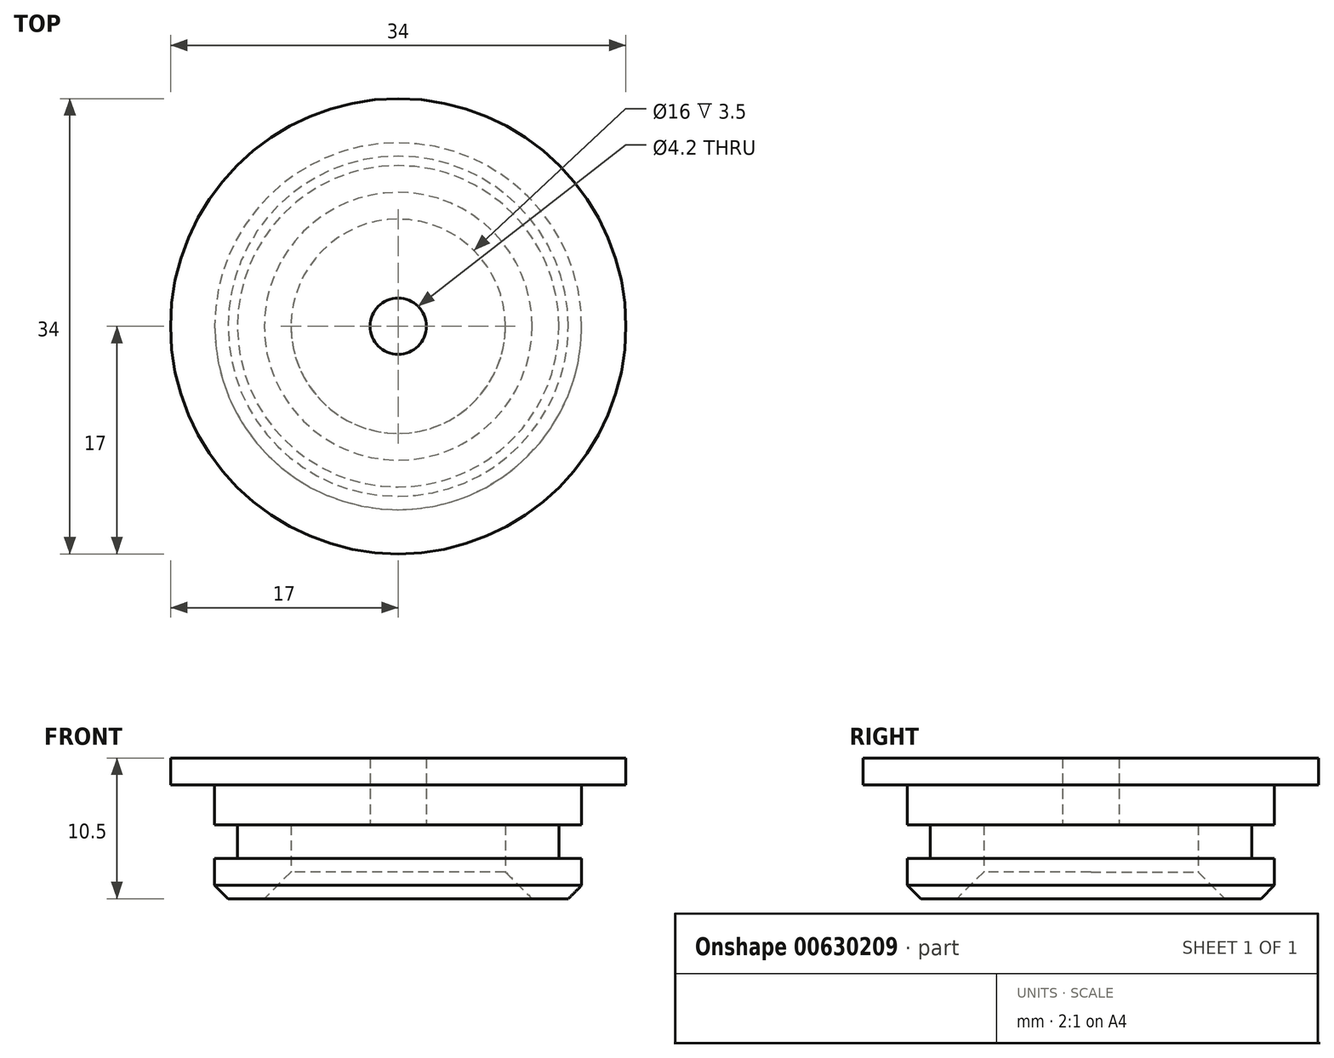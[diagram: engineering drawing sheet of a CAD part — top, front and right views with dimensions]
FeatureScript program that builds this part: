
annotation { "Feature Type Name" : "Feature", "Feature Type Description" : "" }
export const myFeature = defineFeature(function(context is Context, id is Id, definition is map)
    precondition{}
    {
        {
            var Q0;
            Q0=qCreatedBy(makeId("Front.planeOp"),FACE);
            var sketch = newSketch(context, id + "F0", { "sketchPlane" : qUnion([Q0])});
            skLineSegment(sketch, "E0", {"start": v(0, 10.5) * mm, "end": v(17, 10.5) * mm});
            skLineSegment(sketch, "E1", {"start": v(17, 10.5) * mm, "end": v(17, 8.5) * mm});
            skLineSegment(sketch, "E2", {"start": v(17, 8.5) * mm, "end": v(13.7, 8.5) * mm});
            skLineSegment(sketch, "E3", {"start": v(13.7, 8.5) * mm, "end": v(13.7, 5.5) * mm});
            skLineSegment(sketch, "E4", {"start": v(13.7, 0) * mm, "end": v(8, 0) * mm});
            skLineSegment(sketch, "E5", {"start": v(8, 0) * mm, "end": v(8, 5.5) * mm});
            skLineSegment(sketch, "E6", {"start": v(13.7, 5.5) * mm, "end": v(12, 5.5) * mm});
            skLineSegment(sketch, "E7", {"start": v(12, 5.5) * mm, "end": v(12, 3) * mm});
            skLineSegment(sketch, "E8", {"start": v(12, 3) * mm, "end": v(13.7, 3) * mm});
            skLineSegment(sketch, "E9.trimOffspring", {"start": v(13.7, 3) * mm, "end": v(13.7, 0) * mm});
            skLineSegment(sketch, "E10", {"start": v(0, 10.5) * mm, "end": v(0, 5.5) * mm});
            skLineSegment(sketch, "E11", {"start": v(0, 5.5) * mm, "end": v(8, 5.5) * mm});
            skLineSegment(sketch, "E12", {"start": v(0, 0) * mm, "end": v(0, 39.32) * mm, "construction": true});
            skSolve(sketch);
        }
        {
            var Q0;
            Q0 = qSketchRegion(id + "F0", true);
            var Q1;
            Q1=sQuery(id+"F0.wireOp",EDGE,"E12");
            revolve(context, id + "F1", {"entities" : qUnion([Q0]), "axis" : qUnion([Q1]), "revolveType" : RevolveType.FULL});
        }
        {
            var Q0;
            Q0=makeQuery(id+"F1.opRevolve","SWEPT_FACE",FACE,{"disambiguationData":[OSD([sQuery(id+"F0.wireOp",EDGE,"E0")])]});
            var sketch = newSketch(context, id + "F2", { "sketchPlane" : qUnion([Q0])});
            skPoint(sketch, "E13", {"position": v(0, 0) * mm});
            skSolve(sketch);
        }
        {
            var Q0;
            Q0=sQuery(id+"F2.wireOp",VERTEX,"E13");
            var Q1;
            Q1=makeQuery(id+"F1.opRevolve","SWEPT_BODY",BODY,{"disambiguationData":[OSD([sQuery(id+"F0.wireOp",EDGE,"E0"),sQuery(id+"F0.wireOp",EDGE,"E1"),sQuery(id+"F0.wireOp",EDGE,"E2"),sQuery(id+"F0.wireOp",EDGE,"E3"),sQuery(id+"F0.wireOp",EDGE,"E4"),sQuery(id+"F0.wireOp",EDGE,"E5"),sQuery(id+"F0.wireOp",EDGE,"E6"),sQuery(id+"F0.wireOp",EDGE,"E7"),sQuery(id+"F0.wireOp",EDGE,"E8"),sQuery(id+"F0.wireOp",EDGE,"E9.trimOffspring"),sQuery(id+"F0.wireOp",EDGE,"E10"),sQuery(id+"F0.wireOp",EDGE,"E11")])]});
            hole(context, id + "F3", {"style" : HoleStyle.SIMPLE, "endStyle" : HoleEndStyle.BLIND, "standardTappedOrClearance" : lookupTablePath({ "standard" : "ISO", "engagement" : "75%", "pitch" : "0.8 mm", "size" : "M5", "type" : "Tapped" }), "standardBlindInLast" : lookupTablePath({ "standard" : "ISO", "engagement" : "75%", "pitch" : "0.8 mm", "size" : "M5", "type" : "Tapped" }), "holeDiameter" : 4.2 * mm, "majorDiameter" : 5 * mm, "showTappedDepth" : true, "holeDepth" : 10 * mm, "tappedDepth" : 7.6 * mm, "tapClearance" : 3, "startFromSketch" : true, "locations" : qUnion([Q0]), "scope" : qUnion([Q1])});
        }
        {
            var Q0;
            Q0=makeQuery(id+"F1.opRevolve","SWEPT_EDGE",EDGE,{"disambiguationData":[OSD([sQuery(id+"F0.wireOp",EDGE,"E4"),sQuery(id+"F0.wireOp",EDGE,"E9.trimOffspring")])]});
            chamfer(context, id + "F4", {"entities" : qUnion([Q0]), "width" : 1 * mm, "tangentPropagation" : true});
        }
        {
            var Q0;
            Q0=makeQuery(id+"F1.opRevolve","SWEPT_EDGE",EDGE,{"disambiguationData":[OSD([sQuery(id+"F0.wireOp",EDGE,"E4"),sQuery(id+"F0.wireOp",EDGE,"E5")])]});
            chamfer(context, id + "F5", {"entities" : qUnion([Q0]), "width" : 2 * mm, "tangentPropagation" : true});
        }
    });
